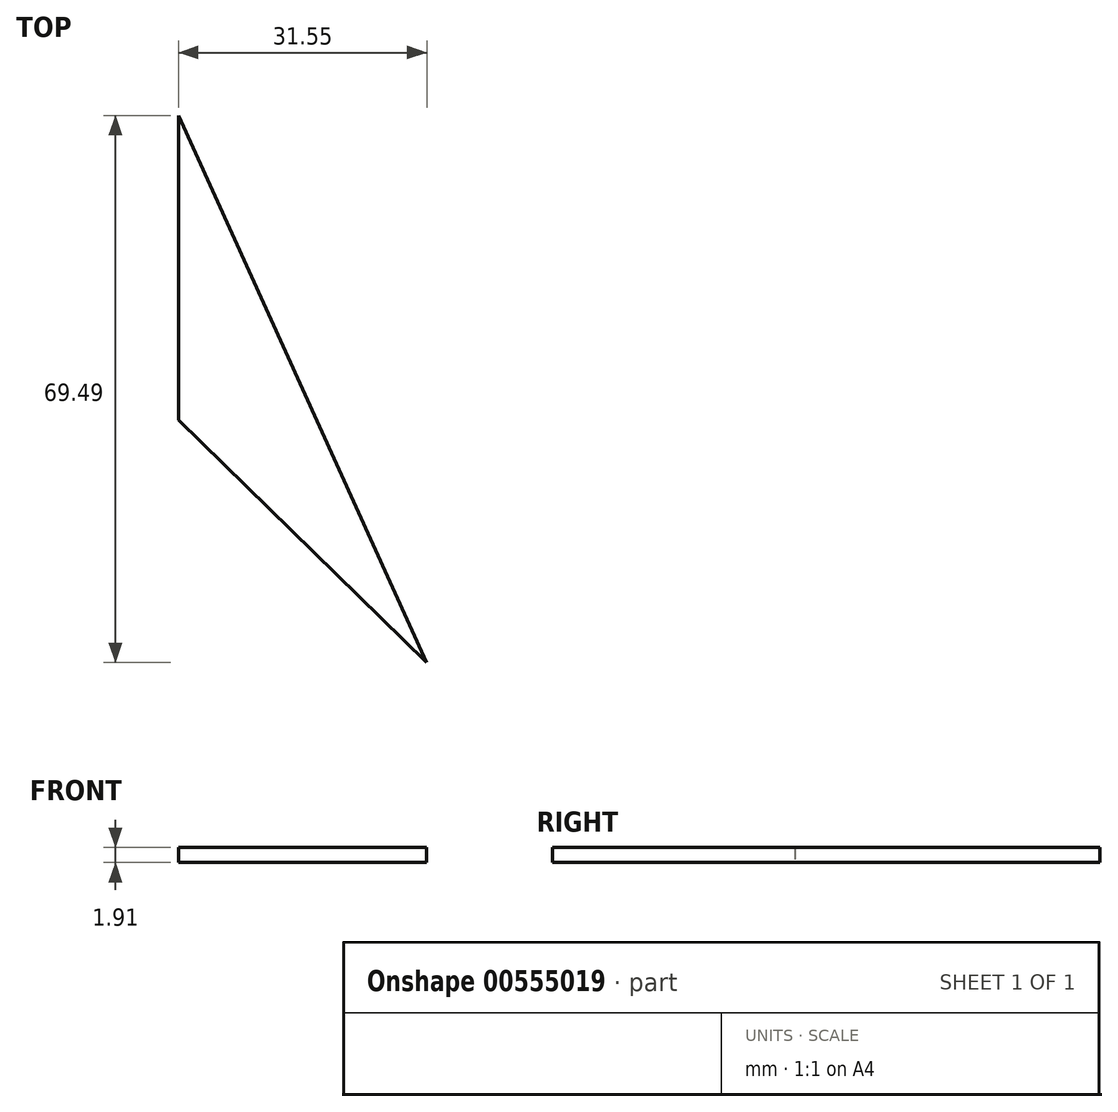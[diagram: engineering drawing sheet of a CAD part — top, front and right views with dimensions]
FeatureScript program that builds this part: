
annotation { "Feature Type Name" : "Feature", "Feature Type Description" : "" }
export const myFeature = defineFeature(function(context is Context, id is Id, definition is map)
    precondition{}
    {
        {
            var Q0;
            Q0=qCreatedBy(makeId("Top.planeOp"),FACE);
            var sketch = newSketch(context, id + "F0", { "sketchPlane" : qUnion([Q0])});
            skLineSegment(sketch, "E0", {"start": v(0, 0) * mm, "end": v(0, 38.7) * mm});
            skLineSegment(sketch, "E1", {"start": v(0, 38.7) * mm, "end": v(31.55, -30.78) * mm});
            skLineSegment(sketch, "E2", {"start": v(0, 0) * mm, "end": v(31.55, -30.78) * mm});
            skSolve(sketch);
        }
        {
            var Q0;
            Q0=makeQuery(id+"F0.imprint","IMPRINT",FACE,{"disambiguationData":[TD([[makeQuery(id+"F0.imprint","IMPRINT",EDGE,{"derivedFrom":sQuery(id+"F0.wireOp",EDGE,"E0")}),-1.0]])]});
            extrude(context, id + "F1", {"entities" : qUnion([Q0]), "depth" : 1.9 * mm, "offsetDistance" : 25.4 * mm});
        }
    });
